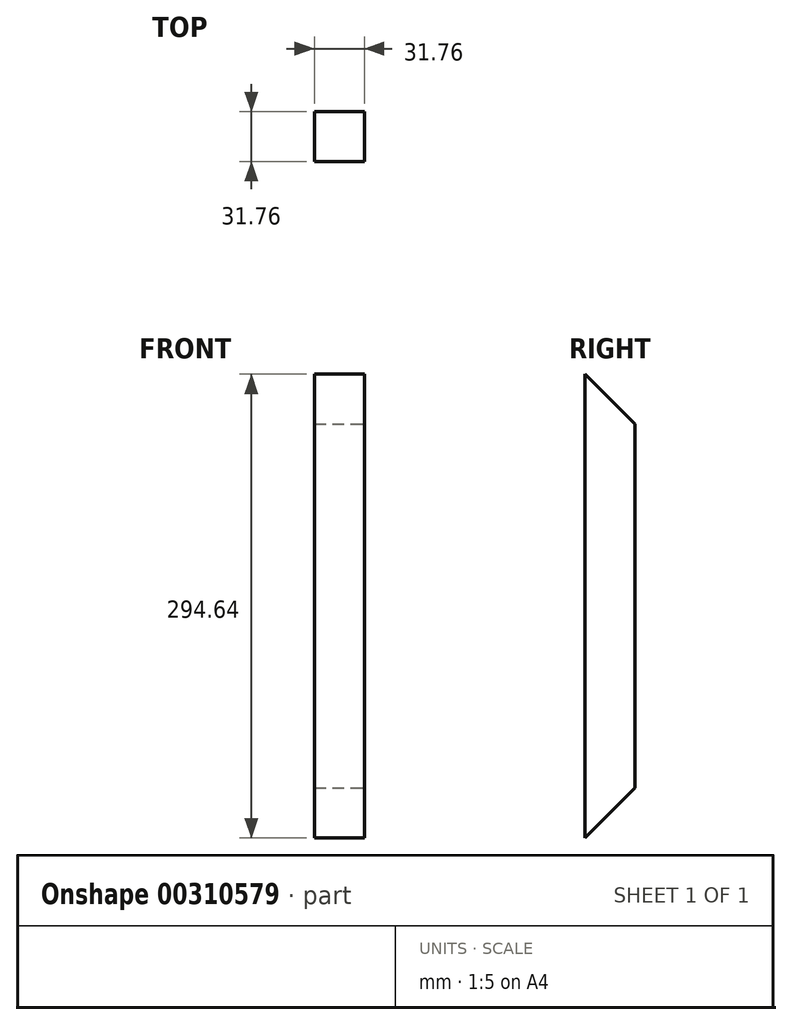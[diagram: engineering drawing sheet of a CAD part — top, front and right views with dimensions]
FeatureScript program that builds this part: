
annotation { "Feature Type Name" : "Feature", "Feature Type Description" : "" }
export const myFeature = defineFeature(function(context is Context, id is Id, definition is map)
    precondition{}
    {
        {
            var Q0;
            Q0=qCreatedBy(makeId("Top.planeOp"),FACE);
            var sketch = newSketch(context, id + "F0", { "sketchPlane" : qUnion([Q0])});
            skLineSegment(sketch, "E0.bottom", {"start": v(15.88, 15.88) * mm, "end": v(-15.88, 15.88) * mm});
            skLineSegment(sketch, "E0.top", {"start": v(15.88, -15.88) * mm, "end": v(-15.88, -15.88) * mm});
            skLineSegment(sketch, "E0.left", {"start": v(15.87, 15.88) * mm, "end": v(15.88, -15.88) * mm});
            skLineSegment(sketch, "E0.right", {"start": v(-15.88, 15.88) * mm, "end": v(-15.88, -15.88) * mm});
            skPoint(sketch, "E0.middle", {"position": v(0, 0) * mm});
            skSolve(sketch);
        }
        {
            var Q0;
            Q0=makeQuery(id+"F0.imprint","IMPRINT",FACE,{"disambiguationData":[TD([[makeQuery(id+"F0.imprint","IMPRINT",EDGE,{"derivedFrom":sQuery(id+"F0.wireOp",EDGE,"E0.bottom")}),1.0]])]});
            extrude(context, id + "F1", {"entities" : qUnion([Q0]), "depth" : 294.64 * mm, "symmetric" : true});
        }
        {
            var Q0;
            Q0=makeQuery(id+"F1.opExtrude","SWEPT_FACE",FACE,{"disambiguationData":[OSD([sQuery(id+"F0.wireOp",EDGE,"E0.left")])]});
            var sketch = newSketch(context, id + "F2", { "sketchPlane" : qUnion([Q0])});
            skLineSegment(sketch, "E1", {"start": v(-15.88, -147.32) * mm, "end": v(15.88, -147.32) * mm});
            skLineSegment(sketch, "E2", {"start": v(15.88, -147.32) * mm, "end": v(15.88, -115.57) * mm});
            skLineSegment(sketch, "E3", {"start": v(15.88, -115.57) * mm, "end": v(-15.88, -147.32) * mm});
            skLineSegment(sketch, "E4.MirrorCS", {"start": v(-15.88, 147.32) * mm, "end": v(15.88, 147.32) * mm});
            skLineSegment(sketch, "E5.MirrorCS", {"start": v(15.88, 115.57) * mm, "end": v(-15.88, 147.32) * mm});
            skLineSegment(sketch, "E6.MirrorCS", {"start": v(15.88, 147.32) * mm, "end": v(15.88, 115.57) * mm});
            skSolve(sketch);
        }
        {
            var Q0;
            Q0 = qSketchRegion(id + "F2", true);
            var Q1;
            Q1=makeQuery(id+"F1.opExtrude","SWEPT_FACE",FACE,{"disambiguationData":[OSD([sQuery(id+"F0.wireOp",EDGE,"E0.right")])]});
            extrude(context, id + "F3", {"entities" : qUnion([Q0]), "operationType" : NewBodyOperationType.REMOVE, "endBound" : BoundingType.UP_TO_SURFACE, "oppositeDirection" : true, "endBoundEntityFace" : qUnion([Q1]), "depth" : 25.4 * mm});
        }
    });
